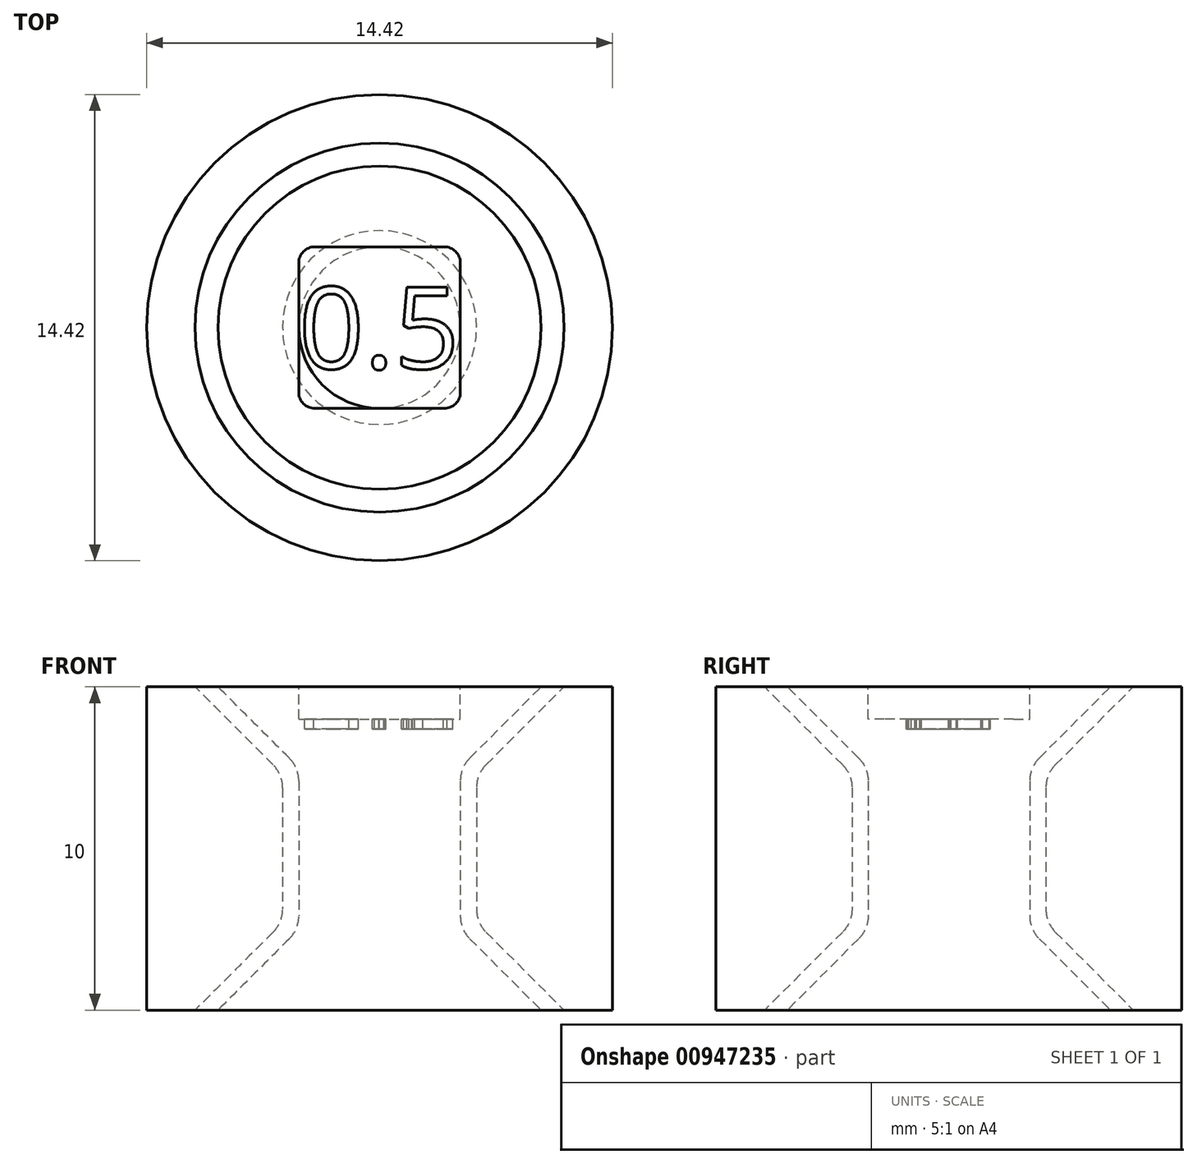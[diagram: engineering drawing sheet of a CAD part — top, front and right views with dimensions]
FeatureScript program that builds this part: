
annotation { "Feature Type Name" : "Feature", "Feature Type Description" : "" }
export const myFeature = defineFeature(function(context is Context, id is Id, definition is map)
    precondition{}
    {
        {
            var Q0;
            Q0=qCreatedBy(makeId("Front.planeOp"),FACE);
            var sketch = newSketch(context, id + "F0", { "sketchPlane" : qUnion([Q0])});
            skLineSegment(sketch, "E0", {"start": v(0, 0) * mm, "end": v(0, 10) * mm});
            skLineSegment(sketch, "E1", {"start": v(0, 10) * mm, "end": v(-5, 10) * mm});
            skLineSegment(sketch, "E2", {"start": v(-5, 10) * mm, "end": v(-2.8, 7.8) * mm});
            skLineSegment(sketch, "E3", {"start": v(-2.5, 7.09) * mm, "end": v(-2.5, 2.91) * mm});
            skLineSegment(sketch, "E4", {"start": v(-2.8, 2.2) * mm, "end": v(-5, 0) * mm});
            skLineSegment(sketch, "E5", {"start": v(-5, 0) * mm, "end": v(0, 0) * mm});
            skLineSegment(sketch, "E6", {"start": v(-7.2, 0) * mm, "end": v(-7.2, 10) * mm});
            skLineSegment(sketch, "E7", {"start": v(-7.2, 10) * mm, "end": v(-5.7, 10) * mm});
            skLineSegment(sketch, "E8", {"start": v(-5.7, 10) * mm, "end": v(-3.3, 7.59) * mm});
            skLineSegment(sketch, "E9", {"start": v(-3, 6.88) * mm, "end": v(-3, 3.12) * mm});
            skLineSegment(sketch, "E10", {"start": v(-3.3, 2.41) * mm, "end": v(-5.7, 0) * mm});
            skLineSegment(sketch, "E11", {"start": v(-5.7, 0) * mm, "end": v(-7.2, 0) * mm});
            skPoint(sketch, "E12.visualSharp", {"position": v(-3, 7.3) * mm});
            skArc(sketch, "E12.filletArc", {"start": v(-3, 6.88) * mm, "mid": v(-3.08, 7.26) * mm, "end": v(-3.3, 7.59) * mm});
            skPoint(sketch, "E13.visualSharp", {"position": v(-2.5, 7.5) * mm});
            skArc(sketch, "E13.filletArc", {"start": v(-2.5, 7.09) * mm, "mid": v(-2.58, 7.47) * mm, "end": v(-2.8, 7.8) * mm});
            skPoint(sketch, "E14.visualSharp", {"position": v(-3, 2.7) * mm});
            skArc(sketch, "E14.filletArc", {"start": v(-3.3, 2.41) * mm, "mid": v(-3.08, 2.74) * mm, "end": v(-3, 3.12) * mm});
            skPoint(sketch, "E15.visualSharp", {"position": v(-2.5, 2.5) * mm});
            skArc(sketch, "E15.filletArc", {"start": v(-2.8, 2.2) * mm, "mid": v(-2.58, 2.53) * mm, "end": v(-2.5, 2.91) * mm});
            skSolve(sketch);
        }
        {
            var Q0;
            Q0=makeQuery(id+"F0.imprint","IMPRINT",FACE,{"disambiguationData":[TD([[makeQuery(id+"F0.imprint","IMPRINT",EDGE,{"derivedFrom":sQuery(id+"F0.wireOp",EDGE,"E0")}),1.0]])]});
            var Q1;
            Q1=makeQuery(id+"F0.imprint","IMPRINT",FACE,{"disambiguationData":[TD([[makeQuery(id+"F0.imprint","IMPRINT",EDGE,{"derivedFrom":sQuery(id+"F0.wireOp",EDGE,"E6")}),-1.0]])]});
            var Q2;
            Q2=sQuery(id+"F0.wireOp",EDGE,"E0");
            revolve(context, id + "F1", {"surfaceOperationType" : NewSurfaceOperationType.NEW, "entities" : qUnion([Q0, Q1]), "axis" : qUnion([Q2]), "revolveType" : RevolveType.FULL});
        }
        {
            var Q0;
            Q0=makeQuery(id+"F1.opRevolve","SWEPT_FACE",FACE,{"disambiguationData":[OSD([sQuery(id+"F0.wireOp",EDGE,"E1")])]});
            cPlane(context, id + "F2", {"entities" : qUnion([Q0]), "cplaneType" : CPlaneType.OFFSET, "offset" : 0 * mm, "width" : 150 * mm, "height" : 150 * mm});
        }
        {
            var Q0;
            Q0=makeQuery(id+"F1.opRevolve","SWEPT_FACE",FACE,{"disambiguationData":[OSD([sQuery(id+"F0.wireOp",EDGE,"E1")])]});
            var sketch = newSketch(context, id + "F3", { "sketchPlane" : qUnion([Q0])});
            skLineSegment(sketch, "E16.bottom", {"start": v(-2, 2.5) * mm, "end": v(2, 2.5) * mm});
            skLineSegment(sketch, "E16.top", {"start": v(-2, -2.5) * mm, "end": v(2, -2.5) * mm});
            skLineSegment(sketch, "E16.left", {"start": v(-2.5, 2) * mm, "end": v(-2.5, -2) * mm});
            skLineSegment(sketch, "E16.right", {"start": v(2.5, 2) * mm, "end": v(2.5, -2) * mm});
            skPoint(sketch, "E17.visualSharp", {"position": v(-2.5, 2.5) * mm});
            skArc(sketch, "E17.filletArc", {"start": v(-2, 2.5) * mm, "mid": v(-2.35, 2.35) * mm, "end": v(-2.5, 2) * mm});
            skPoint(sketch, "E18.visualSharp", {"position": v(-2.5, -2.5) * mm});
            skArc(sketch, "E18.filletArc", {"start": v(-2.5, -2) * mm, "mid": v(-2.35, -2.35) * mm, "end": v(-2, -2.5) * mm});
            skPoint(sketch, "E19.visualSharp", {"position": v(2.5, -2.5) * mm});
            skArc(sketch, "E19.filletArc", {"start": v(2, -2.5) * mm, "mid": v(2.35, -2.35) * mm, "end": v(2.5, -2) * mm});
            skPoint(sketch, "E20.visualSharp", {"position": v(2.5, 2.5) * mm});
            skArc(sketch, "E20.filletArc", {"start": v(2.5, 2) * mm, "mid": v(2.35, 2.35) * mm, "end": v(2, 2.5) * mm});
            skPoint(sketch, "E21", {"position": v(0, 0) * mm});
            skPoint(sketch, "E22", {"position": v(-2.5, 0) * mm});
            skPoint(sketch, "E23", {"position": v(0, 2.5) * mm});
            skSolve(sketch);
        }
        {
            var Q0;
            Q0=makeQuery(id+"F3.imprint","IMPRINT",FACE,{"disambiguationData":[TD([[makeQuery(id+"F3.imprint","IMPRINT",EDGE,{"derivedFrom":sQuery(id+"F3.wireOp",EDGE,"E16.bottom")}),-1.0]])]});
            extrude(context, id + "F4", {"entities" : qUnion([Q0]), "operationType" : NewBodyOperationType.REMOVE, "oppositeDirection" : true, "depth" : 1 * mm, "offsetDistance" : 25 * mm});
        }
        {
            var Q0;
            Q0=qCreatedBy(id+"F2.planeOp",FACE);
            var sketch = newSketch(context, id + "F5", { "sketchPlane" : qUnion([Q0])});
            skText(sketch, "E24", { "text": "0.5", "fontName": "OpenSans-Regular.ttf"});
            skPoint(sketch, "E25", {"position": v(-2.5, 0) * mm});
            const initialGuessF5  = {"E24": [-0.0025, -0.00127, 1, 0, 0.00254]};
            skSetInitialGuess(sketch, initialGuessF5);
            skSolve(sketch);
        }
        {
            var Q0;
            Q0 = qSketchRegion(id + "F5", true);
            extrude(context, id + "F6", {"entities" : qUnion([Q0]), "operationType" : NewBodyOperationType.REMOVE, "oppositeDirection" : true, "depth" : 1.3 * mm, "offsetDistance" : 25 * mm});
        }
    });
